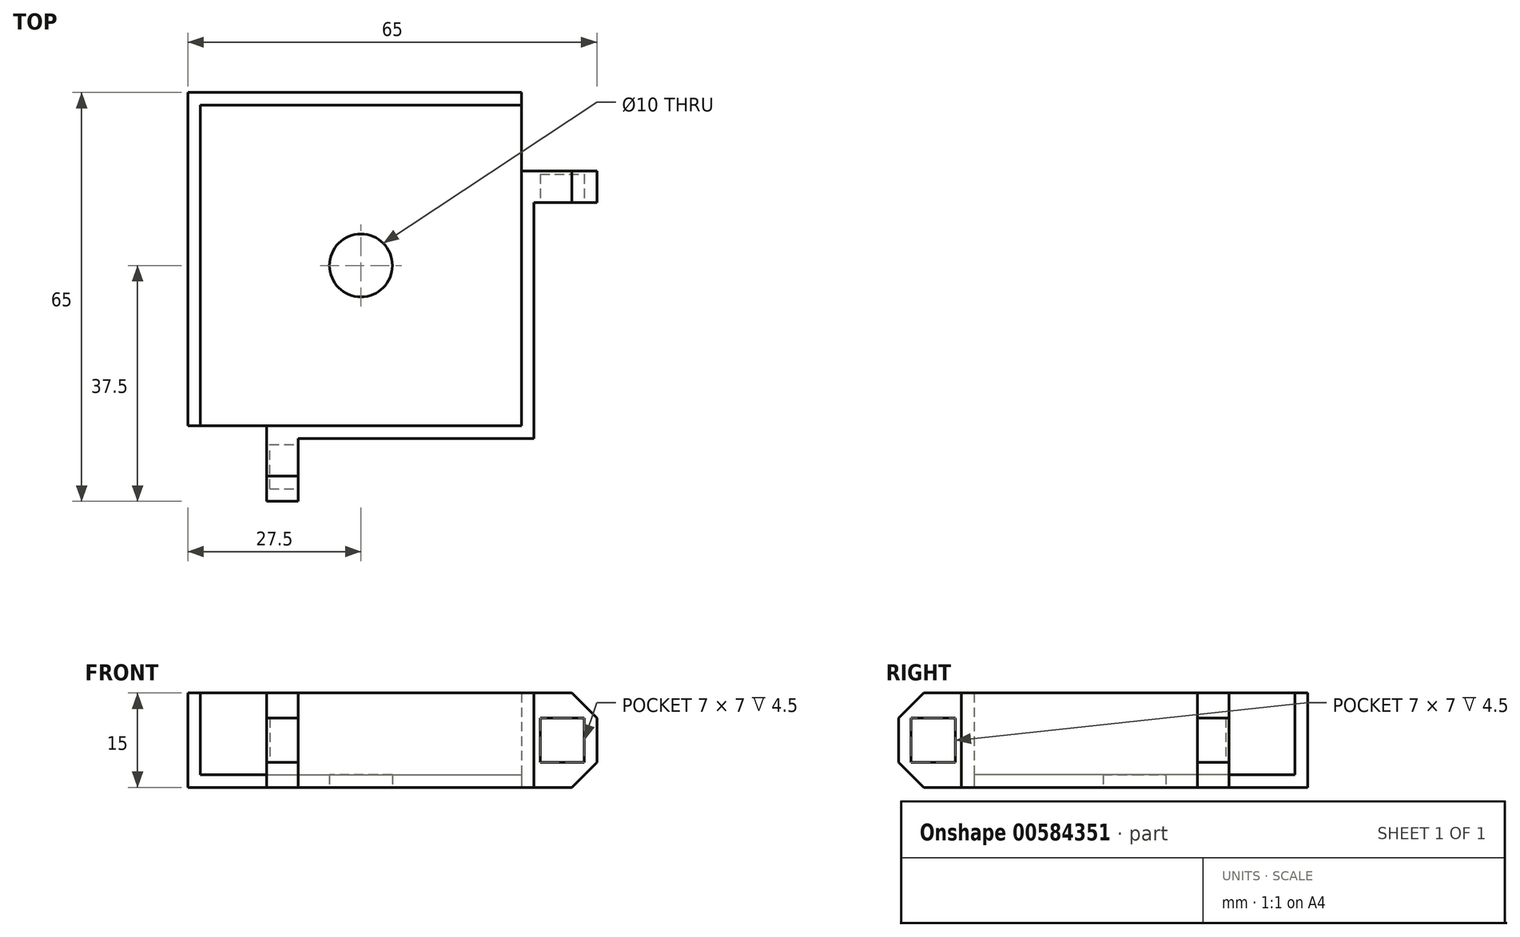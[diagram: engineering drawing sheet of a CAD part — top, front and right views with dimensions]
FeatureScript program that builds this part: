
annotation { "Feature Type Name" : "Feature", "Feature Type Description" : "" }
export const myFeature = defineFeature(function(context is Context, id is Id, definition is map)
    precondition{}
    {
        {
            var Q0;
            Q0=qCreatedBy(makeId("Top.planeOp"),FACE);
            var sketch = newSketch(context, id + "F0", { "sketchPlane" : qUnion([Q0])});
            skLineSegment(sketch, "E0.bottom", {"start": v(-27.5, 27.5) * mm, "end": v(27.5, 27.5) * mm});
            skLineSegment(sketch, "E0.top", {"start": v(-27.5, -27.5) * mm, "end": v(27.5, -27.5) * mm});
            skLineSegment(sketch, "E0.left", {"start": v(-27.5, 27.5) * mm, "end": v(-27.5, -27.5) * mm});
            skLineSegment(sketch, "E0.right", {"start": v(27.5, 27.5) * mm, "end": v(27.5, -27.5) * mm});
            skPoint(sketch, "E0.middle", {"position": v(0, 0) * mm});
            skLineSegment(sketch, "E1.0", {"start": v(-25.5, 25.5) * mm, "end": v(25.5, 25.5) * mm});
            skLineSegment(sketch, "E1.1", {"start": v(-25.5, 25.5) * mm, "end": v(-25.5, -25.5) * mm});
            skLineSegment(sketch, "E1.2", {"start": v(-25.5, -25.5) * mm, "end": v(25.5, -25.5) * mm});
            skLineSegment(sketch, "E1.3", {"start": v(25.5, 25.5) * mm, "end": v(25.5, -25.5) * mm});
            skLineSegment(sketch, "E2", {"start": v(-17.5, -25.5) * mm, "end": v(-17.5, -27.5) * mm});
            skLineSegment(sketch, "E3", {"start": v(-15, -25.5) * mm, "end": v(-15, -27.5) * mm});
            skLineSegment(sketch, "E4", {"start": v(25.5, 17.5) * mm, "end": v(27.5, 17.5) * mm});
            skLineSegment(sketch, "E5", {"start": v(25.5, 15) * mm, "end": v(27.5, 15) * mm});
            skCircle(sketch, "E6", {"center": v(0, 0) * mm, "radius": 5 * mm});
            skLineSegment(sketch, "E7", {"start": v(25.5, 25.5) * mm, "end": v(25.5, 27.5) * mm});
            skLineSegment(sketch, "E8", {"start": v(-25.5, -25.5) * mm, "end": v(-27.5, -25.5) * mm});
            skSolve(sketch);
        }
        {
            var Q0;
            {var subQ4=sQuery(id+"F0.wireOp",EDGE,"E1.0");Q0=makeQuery(id+"F0.imprint","IMPRINT",FACE,{"disambiguationData":[TD([[makeQuery(id+"F0.imprint","IMPRINT",EDGE,{"derivedFrom":subQ4}),-1.0]])]});}
            extrude(context, id + "F1", {"entities" : qUnion([Q0]), "depth" : 2 * mm, "offsetDistance" : 25 * mm});
        }
        {
            var Q0;
            Q0=makeQuery(id+"F0.imprint","IMPRINT",FACE,{"disambiguationData":[TD([[makeQuery(id+"F0.imprint","IMPRINT",EDGE,{"derivedFrom":sQuery(id+"F0.wireOp",EDGE,"E1.0")}),1.0]])]});
            var Q1;
            {var subQ4=sQuery(id+"F0.wireOp",EDGE,"E3");Q1=makeQuery(id+"F0.imprint","IMPRINT",FACE,{"disambiguationData":[TD([[makeQuery(id+"F0.imprint","IMPRINT",EDGE,{"derivedFrom":subQ4}),1.0]])]});}
            extrude(context, id + "F2", {"entities" : qUnion([Q0, Q1]), "operationType" : NewBodyOperationType.ADD, "depth" : 15 * mm, "offsetDistance" : 25 * mm});
        }
        {
            var Q0;
            Q0=makeQuery(id+"F2.opExtrude","SWEPT_FACE",FACE,{"disambiguationData":[OSD([sQuery(id+"F0.wireOp",EDGE,"E0.top")])]});
            var sketch = newSketch(context, id + "F3", { "sketchPlane" : qUnion([Q0])});
            skLineSegment(sketch, "E9", {"start": v(-10, 15) * mm, "end": v(-10, 0) * mm});
            skSolve(sketch);
        }
        {
            var Q0;
            {var subQ0=sQuery(id+"F3.wireOp",EDGE,"E9");Q0=makeQuery(id+"F3.imprint","IMPRINT",FACE,{"disambiguationData":[TD([[makeQuery(id+"F3.imprint","IMPRINT",EDGE,{"derivedFrom":subQ0}),-1.0]])]});}
            extrude(context, id + "F4", {"entities" : qUnion([Q0]), "operationType" : NewBodyOperationType.ADD, "depth" : 10 * mm, "offsetDistance" : 25 * mm});
        }
        {
            var Q0;
            {var subQ0=sQuery(id+"F0.wireOp",EDGE,"E0.top");var subQ1=makeQuery(id+"F2.opExtrude","CAP_EDGE",EDGE,{"disambiguationData":[OSD([subQ0])],"isStart":false});Q0=makeQuery(id+"F4.opExtrude","CAP_EDGE",EDGE,{"disambiguationData":[OSD([subQ0]),TDD([makeQuery(id+"F3.imprint","IMPRINT",EDGE,{"disambiguationData":[TD([[makeQuery(id+"F3.imprint","INTERSECT",VERTEX,{"derivedFrom":[subQ1,sQuery(id+"F3.wireOp",EDGE,"E9")]}),1.0]])],"derivedFrom":subQ1})])],"isStart":false});}
            var Q1;
            {var subQ0=sQuery(id+"F0.wireOp",EDGE,"E0.top");var subQ1=makeQuery(id+"F2.opExtrude","CAP_EDGE",EDGE,{"disambiguationData":[OSD([subQ0])],"isStart":true});Q1=makeQuery(id+"F4.opExtrude","CAP_EDGE",EDGE,{"disambiguationData":[OSD([subQ0]),TDD([makeQuery(id+"F3.imprint","IMPRINT",EDGE,{"disambiguationData":[TD([[makeQuery(id+"F3.imprint","INTERSECT",VERTEX,{"derivedFrom":[subQ1,sQuery(id+"F3.wireOp",EDGE,"E9")]}),1.0]])],"derivedFrom":subQ1})])],"isStart":false});}
            chamfer(context, id + "F5", {"entities" : qUnion([Q0, Q1]), "width" : 4 * mm, "tangentPropagation" : true});
        }
        {
            var Q0;
            Q0=makeQuery(id+"F4.opExtrude","SWEPT_FACE",FACE,{"disambiguationData":[OSD([sQuery(id+"F3.wireOp",EDGE,"E9")])]});
            var sketch = newSketch(context, id + "F6", { "sketchPlane" : qUnion([Q0])});
            skPoint(sketch, "E10", {"position": v(-32, 7.5) * mm});
            skLineSegment(sketch, "E11.bottom", {"start": v(-35.5, 11) * mm, "end": v(-28.5, 11) * mm});
            skLineSegment(sketch, "E11.top", {"start": v(-35.5, 4) * mm, "end": v(-28.5, 4) * mm});
            skLineSegment(sketch, "E11.left", {"start": v(-35.5, 11) * mm, "end": v(-35.5, 4) * mm});
            skLineSegment(sketch, "E11.right", {"start": v(-28.5, 11) * mm, "end": v(-28.5, 4) * mm});
            skPoint(sketch, "E12", {"position": v(-27.5, 7.5) * mm});
            skSolve(sketch);
        }
        {
            var Q0;
            Q0=makeQuery(id+"F6.imprint","IMPRINT",FACE,{"disambiguationData":[TD([[makeQuery(id+"F6.imprint","IMPRINT",EDGE,{"derivedFrom":sQuery(id+"F6.wireOp",EDGE,"E11.bottom")}),-1.0]])]});
            extrude(context, id + "F7", {"entities" : qUnion([Q0]), "operationType" : NewBodyOperationType.REMOVE, "oppositeDirection" : true, "depth" : 4.5 * mm, "offsetDistance" : 25 * mm});
        }
        {
            var Q0;
            Q0=makeQuery(id+"F2.opExtrude","SWEPT_FACE",FACE,{"disambiguationData":[OSD([sQuery(id+"F0.wireOp",EDGE,"E0.right")])]});
            var sketch = newSketch(context, id + "F8", { "sketchPlane" : qUnion([Q0])});
            skLineSegment(sketch, "E13", {"start": v(10, 15) * mm, "end": v(10, 0) * mm});
            skSolve(sketch);
        }
        {
            var Q0;
            {var subQ0=sQuery(id+"F8.wireOp",EDGE,"E13");Q0=makeQuery(id+"F8.imprint","IMPRINT",FACE,{"disambiguationData":[TD([[makeQuery(id+"F8.imprint","IMPRINT",EDGE,{"derivedFrom":subQ0}),1.0]])]});}
            extrude(context, id + "F9", {"entities" : qUnion([Q0]), "operationType" : NewBodyOperationType.ADD, "depth" : 10 * mm, "offsetDistance" : 25 * mm});
        }
        {
            var Q0;
            Q0=makeQuery(id+"F9.opExtrude","SWEPT_FACE",FACE,{"disambiguationData":[OSD([sQuery(id+"F8.wireOp",EDGE,"E13")])]});
            var sketch = newSketch(context, id + "F10", { "sketchPlane" : qUnion([Q0])});
            skPoint(sketch, "E14", {"position": v(32, 7.5) * mm});
            skLineSegment(sketch, "E15.bottom", {"start": v(28.5, 11) * mm, "end": v(35.5, 11) * mm});
            skLineSegment(sketch, "E15.top", {"start": v(28.5, 4) * mm, "end": v(35.5, 4) * mm});
            skLineSegment(sketch, "E15.left", {"start": v(28.5, 11) * mm, "end": v(28.5, 4) * mm});
            skLineSegment(sketch, "E15.right", {"start": v(35.5, 11) * mm, "end": v(35.5, 4) * mm});
            skPoint(sketch, "E16", {"position": v(27.5, 7.5) * mm});
            skSolve(sketch);
        }
        {
            var Q0;
            Q0=makeQuery(id+"F10.imprint","IMPRINT",FACE,{"disambiguationData":[TD([[makeQuery(id+"F10.imprint","IMPRINT",EDGE,{"derivedFrom":sQuery(id+"F10.wireOp",EDGE,"E15.bottom")}),-1.0]])]});
            extrude(context, id + "F11", {"entities" : qUnion([Q0]), "operationType" : NewBodyOperationType.REMOVE, "oppositeDirection" : true, "depth" : 4.5 * mm, "offsetDistance" : 25 * mm});
        }
        {
            var Q0;
            {var subQ0=sQuery(id+"F0.wireOp",EDGE,"E0.right");var subQ1=makeQuery(id+"F2.opExtrude","CAP_EDGE",EDGE,{"disambiguationData":[OSD([subQ0])],"isStart":false});Q0=makeQuery(id+"F9.opExtrude","CAP_EDGE",EDGE,{"disambiguationData":[OSD([subQ0]),TDD([makeQuery(id+"F8.imprint","IMPRINT",EDGE,{"disambiguationData":[TD([[makeQuery(id+"F8.imprint","INTERSECT",VERTEX,{"derivedFrom":[subQ1,sQuery(id+"F8.wireOp",EDGE,"E13")]}),1.0]])],"derivedFrom":subQ1})])],"isStart":false});}
            var Q1;
            {var subQ0=sQuery(id+"F0.wireOp",EDGE,"E0.right");var subQ1=makeQuery(id+"F2.opExtrude","CAP_EDGE",EDGE,{"disambiguationData":[OSD([subQ0])],"isStart":true});Q1=makeQuery(id+"F9.opExtrude","CAP_EDGE",EDGE,{"disambiguationData":[OSD([subQ0]),TDD([makeQuery(id+"F8.imprint","IMPRINT",EDGE,{"disambiguationData":[TD([[makeQuery(id+"F8.imprint","INTERSECT",VERTEX,{"derivedFrom":[subQ1,sQuery(id+"F8.wireOp",EDGE,"E13")]}),1.0]])],"derivedFrom":subQ1})])],"isStart":false});}
            chamfer(context, id + "F12", {"entities" : qUnion([Q0, Q1]), "width" : 4 * mm, "tangentPropagation" : true});
        }
    });
